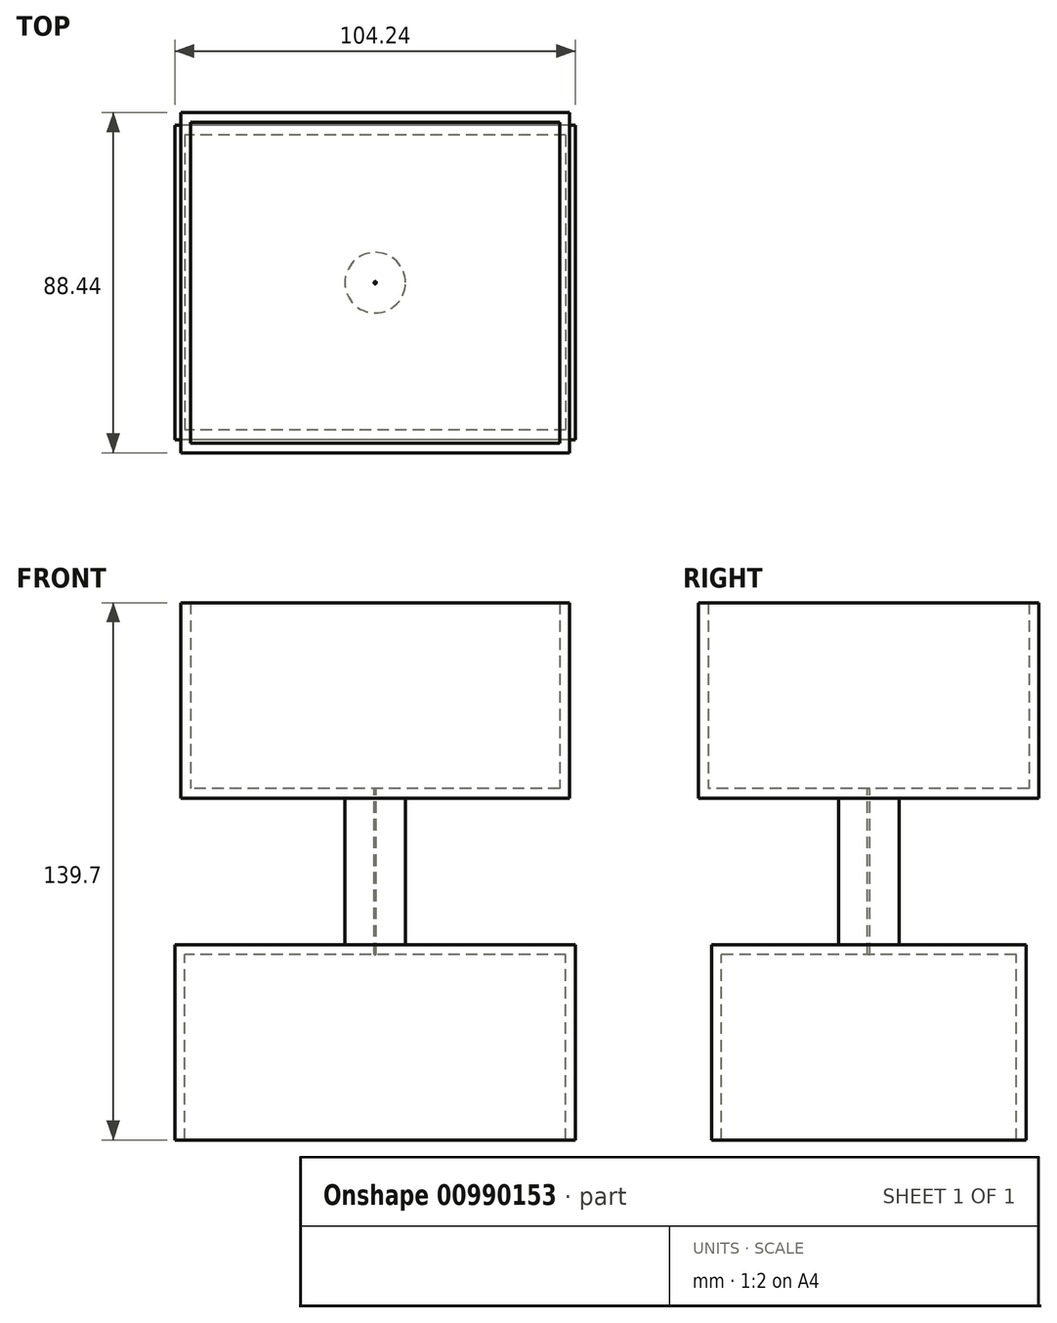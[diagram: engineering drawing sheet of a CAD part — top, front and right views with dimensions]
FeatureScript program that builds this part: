
annotation { "Feature Type Name" : "Feature", "Feature Type Description" : "" }
export const myFeature = defineFeature(function(context is Context, id is Id, definition is map)
    precondition{}
    {
        {
            var Q0;
            Q0=qCreatedBy(makeId("Top.planeOp"),FACE);
            var sketch = newSketch(context, id + "F0", { "sketchPlane" : qUnion([Q0])});
            skLineSegment(sketch, "E0.bottom", {"start": v(50.52, 44.22) * mm, "end": v(-50.52, 44.22) * mm});
            skLineSegment(sketch, "E0.top", {"start": v(50.52, -44.22) * mm, "end": v(-50.52, -44.22) * mm});
            skLineSegment(sketch, "E0.left", {"start": v(50.52, 44.22) * mm, "end": v(50.52, -44.22) * mm});
            skLineSegment(sketch, "E0.right", {"start": v(-50.52, 44.22) * mm, "end": v(-50.52, -44.22) * mm});
            skPoint(sketch, "E0.middle", {"position": v(0, 0) * mm});
            skSolve(sketch);
        }
        {
            var Q0;
            Q0=makeQuery(id+"F0.imprint","IMPRINT",FACE,{"disambiguationData":[TD([[makeQuery(id+"F0.imprint","IMPRINT",EDGE,{"derivedFrom":sQuery(id+"F0.wireOp",EDGE,"E0.bottom")}),1.0]])]});
            extrude(context, id + "F1", {"entities" : qUnion([Q0]), "depth" : 50.8 * mm, "offsetDistance" : 25.4 * mm});
        }
        {
            var Q0;
            Q0=makeQuery(id+"F1.opExtrude","CAP_FACE",FACE,{"disambiguationData":[OSD([sQuery(id+"F0.wireOp",EDGE,"E0.bottom"),sQuery(id+"F0.wireOp",EDGE,"E0.top"),sQuery(id+"F0.wireOp",EDGE,"E0.left"),sQuery(id+"F0.wireOp",EDGE,"E0.right")])],"isStart":false});
            shell(context, id + "F2", {"entities" : qUnion([Q0]), "thickness" : 2.54 * mm});
        }
        {
            var Q0;
            Q0=makeQuery(id+"F1.opExtrude","CAP_FACE",FACE,{"disambiguationData":[OSD([sQuery(id+"F0.wireOp",EDGE,"E0.bottom"),sQuery(id+"F0.wireOp",EDGE,"E0.top"),sQuery(id+"F0.wireOp",EDGE,"E0.left"),sQuery(id+"F0.wireOp",EDGE,"E0.right")])],"isStart":true});
            var sketch = newSketch(context, id + "F3", { "sketchPlane" : qUnion([Q0])});
            skCircle(sketch, "E1", {"center": v(0, 0) * mm, "radius": 7.88 * mm});
            skSolve(sketch);
        }
        {
            var Q0;
            Q0=makeQuery(id+"F3.imprint","IMPRINT",FACE,{"disambiguationData":[TD([[makeQuery(id+"F3.imprint","IMPRINT",EDGE,{"derivedFrom":sQuery(id+"F3.wireOp",EDGE,"E1")}),1.0]])]});
            extrude(context, id + "F4", {"entities" : qUnion([Q0]), "operationType" : NewBodyOperationType.ADD, "depth" : 38.1 * mm, "offsetDistance" : 25.4 * mm});
        }
        {
            var Q0;
            Q0=makeQuery(id+"F2.opShell","OFFSET_FACE",FACE,{"disambiguationData":[OSD([sQuery(id+"F0.wireOp",EDGE,"E0.bottom"),sQuery(id+"F0.wireOp",EDGE,"E0.top"),sQuery(id+"F0.wireOp",EDGE,"E0.left"),sQuery(id+"F0.wireOp",EDGE,"E0.right")])]});
            var sketch = newSketch(context, id + "F5", { "sketchPlane" : qUnion([Q0])});
            skCircle(sketch, "E2", {"center": v(0, 0) * mm, "radius": 2.97 * mm});
            skSolve(sketch);
        }
        {
            var Q0;
            Q0=sQuery(id+"F5.wireOp",VERTEX,"E2.center");
            var Q1;
            Q1=makeQuery(id+"F1.opExtrude","SWEPT_BODY",BODY,{"disambiguationData":[OSD([sQuery(id+"F0.wireOp",EDGE,"E0.bottom"),sQuery(id+"F0.wireOp",EDGE,"E0.top"),sQuery(id+"F0.wireOp",EDGE,"E0.left"),sQuery(id+"F0.wireOp",EDGE,"E0.right")])]});
            hole(context, id + "F6", {"style" : HoleStyle.SIMPLE, "endStyle" : HoleEndStyle.THROUGH, "holeDiameter" : 0.6 * mm, "majorDiameter" : 6.35 * mm, "isTappedThrough" : true, "tappedDepth" : 12.7 * mm, "tapClearance" : 3, "locations" : qUnion([Q0]), "scope" : qUnion([Q1])});
        }
        {
            var Q0;
            Q0=makeQuery(id+"F4.opExtrude","CAP_FACE",FACE,{"disambiguationData":[OSD([sQuery(id+"F3.wireOp",EDGE,"E1")])],"isStart":false});
            var sketch = newSketch(context, id + "F7", { "sketchPlane" : qUnion([Q0])});
            skLineSegment(sketch, "E3.bottom", {"start": v(52.12, -40.9) * mm, "end": v(-52.12, -40.9) * mm});
            skLineSegment(sketch, "E3.top", {"start": v(52.12, 40.9) * mm, "end": v(-52.12, 40.9) * mm});
            skLineSegment(sketch, "E3.left", {"start": v(52.12, -40.9) * mm, "end": v(52.12, 40.9) * mm});
            skLineSegment(sketch, "E3.right", {"start": v(-52.12, -40.9) * mm, "end": v(-52.12, 40.9) * mm});
            skPoint(sketch, "E3.middle", {"position": v(0, 0) * mm});
            skSolve(sketch);
        }
        {
            var Q0;
            Q0=makeQuery(id+"F7.imprint","IMPRINT",FACE,{"disambiguationData":[TD([[makeQuery(id+"F7.imprint","IMPRINT",EDGE,{"derivedFrom":sQuery(id+"F7.wireOp",EDGE,"E3.bottom")}),-1.0]])]});
            extrude(context, id + "F8", {"entities" : qUnion([Q0]), "depth" : 50.8 * mm, "offsetDistance" : 25.4 * mm});
        }
        {
            var Q0;
            Q0=makeQuery(id+"F8.opExtrude","CAP_FACE",FACE,{"disambiguationData":[OSD([sQuery(id+"F3.wireOp",EDGE,"E1"),sQuery(id+"F7.wireOp",EDGE,"E3.bottom"),sQuery(id+"F7.wireOp",EDGE,"E3.top"),sQuery(id+"F7.wireOp",EDGE,"E3.left"),sQuery(id+"F7.wireOp",EDGE,"E3.right")])],"isStart":false});
            shell(context, id + "F9", {"entities" : qUnion([Q0]), "thickness" : 2.54 * mm});
        }
        {
            var Q0;
            {var subQ0=sQuery(id+"F7.wireOp",EDGE,"E3.right");var subQ1=sQuery(id+"F7.wireOp",EDGE,"E3.left");var subQ2=sQuery(id+"F7.wireOp",EDGE,"E3.top");var subQ3=sQuery(id+"F7.wireOp",EDGE,"E3.bottom");var subQ4=sQuery(id+"F3.wireOp",EDGE,"E1");Q0=makeQuery(id+"F9.opShell","OFFSET_FACE",FACE,{"disambiguationData":[OSD([subQ4,subQ3,subQ2,subQ1,subQ0]),TDD([makeQuery(id+"F8.opExtrude","CAP_FACE",FACE,{"disambiguationData":[OSD([subQ4,subQ3,subQ2,subQ1,subQ0])],"isStart":false})])]});}
            extrude(context, id + "F10", {"entities" : qUnion([Q0]), "operationType" : NewBodyOperationType.REMOVE, "oppositeDirection" : true, "depth" : 48.26 * mm, "offsetDistance" : 25.4 * mm});
        }
        {
            var Q0;
            Q0=makeQuery(id+"F4.opExtrude","CAP_FACE",FACE,{"disambiguationData":[OSD([sQuery(id+"F3.wireOp",EDGE,"E1")])],"isStart":false});
            extrude(context, id + "F11", {"entities" : qUnion([Q0]), "operationType" : NewBodyOperationType.ADD, "depth" : 2.54 * mm, "offsetDistance" : 25.4 * mm});
        }
    });
